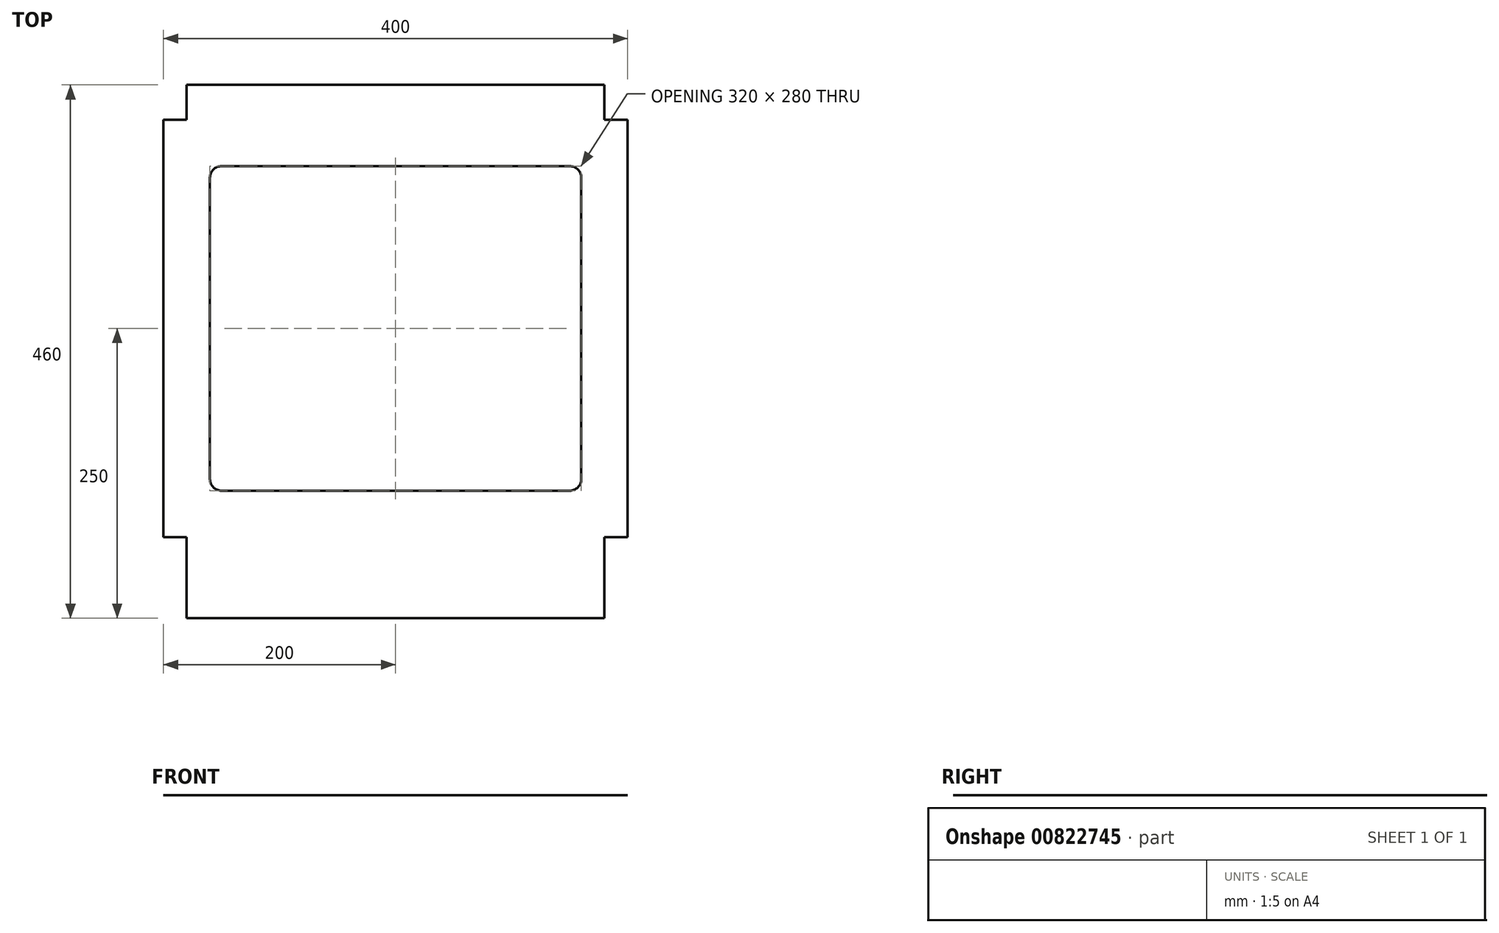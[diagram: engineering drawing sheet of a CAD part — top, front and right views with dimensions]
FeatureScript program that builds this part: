
annotation { "Feature Type Name" : "Feature", "Feature Type Description" : "" }
export const myFeature = defineFeature(function(context is Context, id is Id, definition is map)
    precondition{}
    {
        {
            var Q0;
            Q0=qCreatedBy(makeId("Top.planeOp"),FACE);
            var sketch = newSketch(context, id + "F0", { "sketchPlane" : qUnion([Q0])});
            skPoint(sketch, "E0.middle", {"position": v(0, 0) * mm});
            skLineSegment(sketch, "E1", {"start": v(-200, -180) * mm, "end": v(-180, -180) * mm});
            skLineSegment(sketch, "E2", {"start": v(-180, 180) * mm, "end": v(-200, 180) * mm});
            skLineSegment(sketch, "E3", {"start": v(-180, 180) * mm, "end": v(-180, 210) * mm});
            skLineSegment(sketch, "E4", {"start": v(0, 25) * mm, "end": v(0, -25) * mm, "construction": true});
            skLineSegment(sketch, "E5", {"start": v(-200, 180) * mm, "end": v(-200, -180) * mm});
            skLineSegment(sketch, "E6", {"start": v(0, 25) * mm, "end": v(0, 210) * mm, "construction": true});
            skPoint(sketch, "E7", {"position": v(0, 210) * mm});
            skLineSegment(sketch, "E8.bottom", {"start": v(0, -140) * mm, "end": v(-150, -140) * mm});
            skLineSegment(sketch, "E8.top", {"start": v(0, 140) * mm, "end": v(-150, 140) * mm});
            skLineSegment(sketch, "E8.right", {"start": v(-160, -130) * mm, "end": v(-160, 130) * mm});
            skPoint(sketch, "E9.visualSharp", {"position": v(-160, 140) * mm});
            skArc(sketch, "E9.filletArc", {"start": v(-150, 140) * mm, "mid": v(-157.07, 137.07) * mm, "end": v(-160, 130) * mm});
            skPoint(sketch, "E10.visualSharp", {"position": v(-160, -140) * mm});
            skArc(sketch, "E10.filletArc", {"start": v(-160, -130) * mm, "mid": v(-157.07, -137.07) * mm, "end": v(-150, -140) * mm});
            skLineSegment(sketch, "E11", {"start": v(-180, -180) * mm, "end": v(-180, -250) * mm});
            skLineSegment(sketch, "E12", {"start": v(-180, 210) * mm, "end": v(0, 210) * mm});
            skLineSegment(sketch, "E13", {"start": v(-180, -250) * mm, "end": v(0, -250) * mm});
            skLineSegment(sketch, "E14", {"start": v(0, -25) * mm, "end": v(0, -250) * mm});
            skLineSegment(sketch, "E15.MirrorCS", {"start": v(180, 210) * mm, "end": v(0, 210) * mm});
            skLineSegment(sketch, "E16.MirrorCS", {"start": v(180, 180) * mm, "end": v(180, 210) * mm});
            skLineSegment(sketch, "E17.MirrorCS", {"start": v(180, 180) * mm, "end": v(200, 180) * mm});
            skLineSegment(sketch, "E18.MirrorCS", {"start": v(200, 180) * mm, "end": v(200, -180) * mm});
            skLineSegment(sketch, "E19.MirrorCS", {"start": v(200, -180) * mm, "end": v(180, -180) * mm});
            skLineSegment(sketch, "E20.MirrorCS", {"start": v(180, -180) * mm, "end": v(180, -250) * mm});
            skLineSegment(sketch, "E21.MirrorCS", {"start": v(180, -250) * mm, "end": v(0, -250) * mm});
            skLineSegment(sketch, "E22.MirrorCS", {"start": v(0, -140) * mm, "end": v(150, -140) * mm});
            skArc(sketch, "E23.MirrorCS", {"start": v(160, -130) * mm, "mid": v(157.07, -137.07) * mm, "end": v(150, -140) * mm});
            skLineSegment(sketch, "E24.MirrorCS", {"start": v(160, -130) * mm, "end": v(160, 130) * mm});
            skArc(sketch, "E25.MirrorCS", {"start": v(150, 140) * mm, "mid": v(157.07, 137.07) * mm, "end": v(160, 130) * mm});
            skLineSegment(sketch, "E26.MirrorCS", {"start": v(0, 140) * mm, "end": v(150, 140) * mm});
            skSolve(sketch);
        }
        {
            var Q0;
            Q0=qSketchRegion(id+"F0",true);
            extrude(context, id + "F1", {"entities" : qUnion([Q0]), "depth" : 1 / 406.4 * mm, "offsetDistance" : 25 * mm});
        }
        {
            var Q0;
            Q0=makeQuery(id+"F0.imprint","IMPRINT",FACE,{"disambiguationData":[TD([[makeQuery(id+"F0.imprint","IMPRINT",EDGE,{"derivedFrom":sQuery(id+"F0.wireOp",EDGE,"E8.bottom")}),-1.0]])]});
            extrude(context, id + "F2", {"entities" : qUnion([Q0]), "depth" : 1 / 406.4 * mm, "offsetDistance" : 25 * mm});
        }
    });
